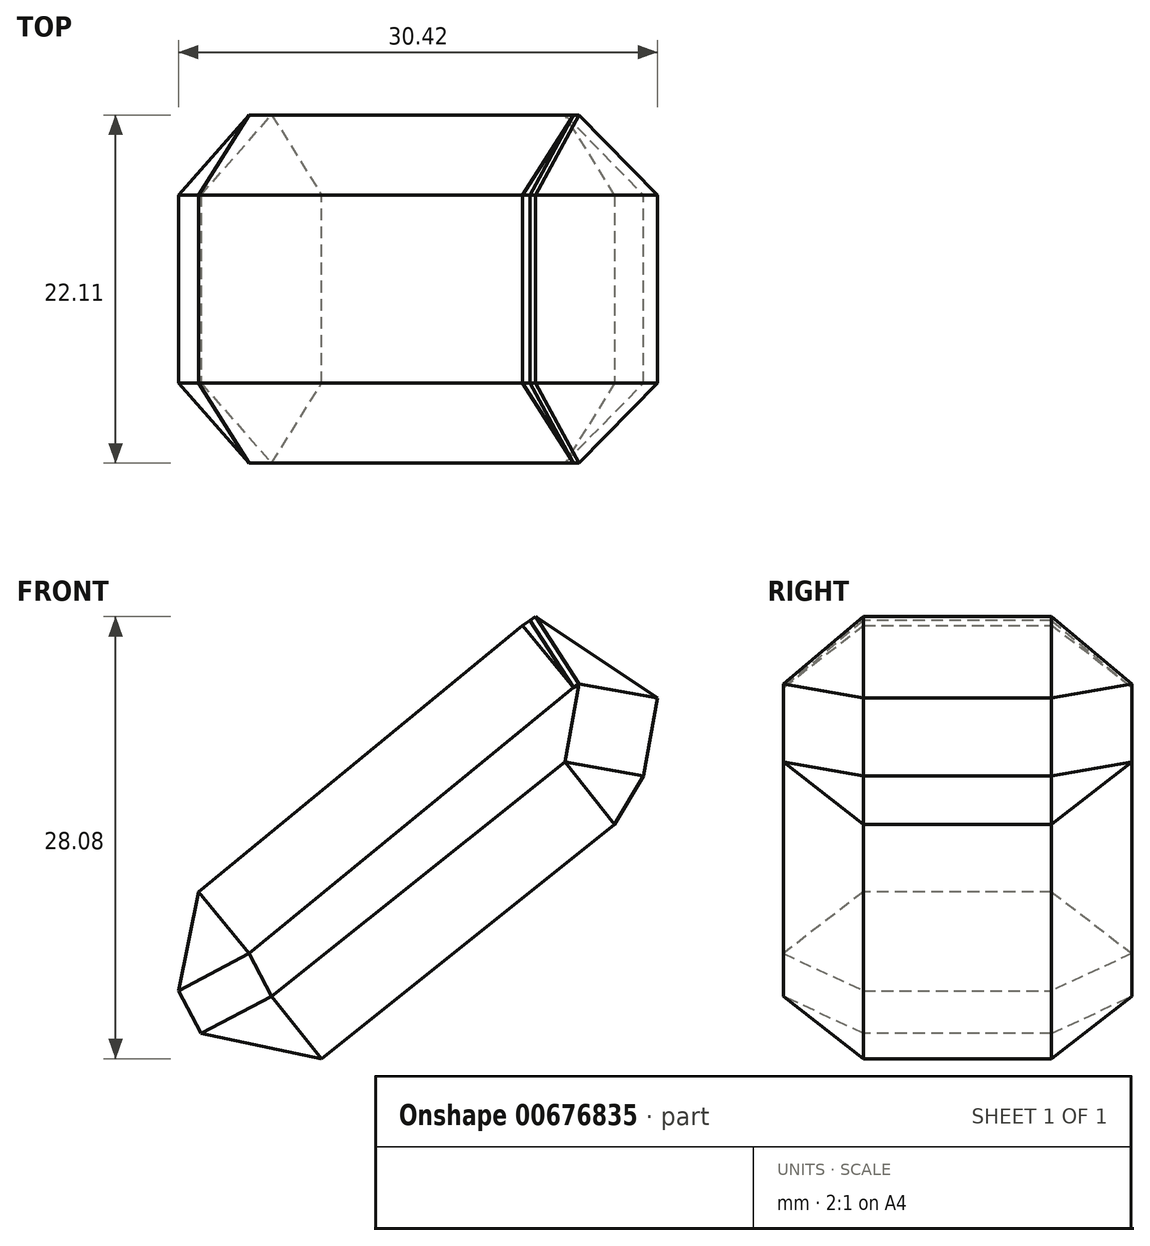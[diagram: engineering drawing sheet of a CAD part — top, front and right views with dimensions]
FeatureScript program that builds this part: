
annotation { "Feature Type Name" : "Feature", "Feature Type Description" : "" }
export const myFeature = defineFeature(function(context is Context, id is Id, definition is map)
    precondition{}
    {
        {
            var Q0;
            Q0=qCreatedBy(makeId("Front.planeOp"),FACE);
            var sketch = newSketch(context, id + "F0", { "sketchPlane" : qUnion([Q0])});
            skLineSegment(sketch, "E0", {"start": v(6.49, 21.97) * mm, "end": v(-20.54, -37.5) * mm});
            skLineSegment(sketch, "E1", {"start": v(-20.54, -37.5) * mm, "end": v(0, 0) * mm});
            skLineSegment(sketch, "E2", {"start": v(0, 0) * mm, "end": v(11.4, 42.9) * mm});
            skLineSegment(sketch, "E3", {"start": v(11.4, 42.9) * mm, "end": v(6.49, 21.97) * mm});
            skLineSegment(sketch, "E4", {"start": v(81.14, -36.27) * mm, "end": v(70.14, -43.37) * mm});
            skLineSegment(sketch, "E5", {"start": v(70.14, -43.37) * mm, "end": v(46.13, -63.08) * mm});
            skLineSegment(sketch, "E6", {"start": v(46.13, -63.08) * mm, "end": v(52.36, -74.9) * mm});
            skLineSegment(sketch, "E7", {"start": v(52.36, -74.9) * mm, "end": v(77.26, -54.99) * mm});
            skLineSegment(sketch, "E8", {"start": v(77.26, -54.99) * mm, "end": v(80.98, -34.44) * mm});
            skSolve(sketch);
        }
        {
            var Q0;
            {var subQ1=sQuery(id+"F0.wireOp",EDGE,"E5");Q0=makeQuery(id+"F0.imprint","IMPRINT",FACE,{"disambiguationData":[TD([[makeQuery(id+"F0.imprint","IMPRINT",EDGE,{"derivedFrom":subQ1}),1.0]])]});}
            extrude(context, id + "F1", {"entities" : qUnion([Q0]), "oppositeDirection" : true, "depth" : 22.1 * mm, "offsetDistance" : 25.4 * mm});
        }
        {
            var Q0;
            Q0=makeQuery(id+"F1.opExtrude","CAP_FACE",FACE,{"disambiguationData":[OSD([sQuery(id+"F0.wireOp",EDGE,"E4"),sQuery(id+"F0.wireOp",EDGE,"E5"),sQuery(id+"F0.wireOp",EDGE,"E6"),sQuery(id+"F0.wireOp",EDGE,"E7"),sQuery(id+"F0.wireOp",EDGE,"E8")])],"isStart":false});
            var Q1;
            Q1=makeQuery(id+"F1.opExtrude","SWEPT_EDGE",EDGE,{"disambiguationData":[OSD([sQuery(id+"F0.wireOp",EDGE,"E7"),sQuery(id+"F0.wireOp",EDGE,"E8")])]});
            var Q2;
            Q2=makeQuery(id+"F1.opExtrude","SWEPT_FACE",FACE,{"disambiguationData":[OSD([sQuery(id+"F0.wireOp",EDGE,"E8")])]});
            var Q3;
            Q3=makeQuery(id+"F1.opExtrude","SWEPT_FACE",FACE,{"disambiguationData":[OSD([sQuery(id+"F0.wireOp",EDGE,"E5")])]});
            var Q4;
            Q4=makeQuery(id+"F1.opExtrude","SWEPT_FACE",FACE,{"disambiguationData":[OSD([sQuery(id+"F0.wireOp",EDGE,"E7")])]});
            var Q5;
            Q5=makeQuery(id+"F1.opExtrude","CAP_FACE",FACE,{"disambiguationData":[OSD([sQuery(id+"F0.wireOp",EDGE,"E4"),sQuery(id+"F0.wireOp",EDGE,"E5"),sQuery(id+"F0.wireOp",EDGE,"E6"),sQuery(id+"F0.wireOp",EDGE,"E7"),sQuery(id+"F0.wireOp",EDGE,"E8")])],"isStart":true});
            chamfer(context, id + "F2", {"entities" : qUnion([Q0, Q1, Q2, Q3, Q4, Q5]), "width" : 5.08 * mm, "tangentPropagation" : true});
        }
    });
